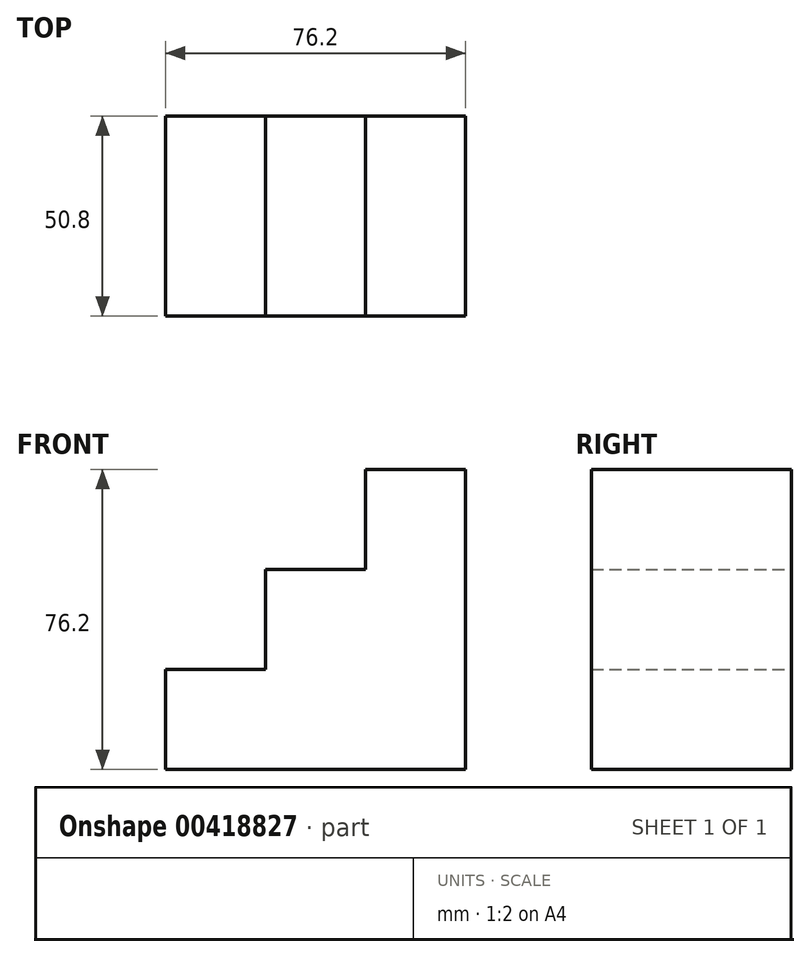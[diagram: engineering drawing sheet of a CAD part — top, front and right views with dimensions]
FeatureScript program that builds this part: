
annotation { "Feature Type Name" : "Feature", "Feature Type Description" : "" }
export const myFeature = defineFeature(function(context is Context, id is Id, definition is map)
    precondition{}
    {
        {
            var Q0;
            Q0=qCreatedBy(makeId("Front.planeOp"),FACE);
            var sketch = newSketch(context, id + "F0", { "sketchPlane" : qUnion([Q0])});
            skLineSegment(sketch, "E0", {"start": v(0, 0) * mm, "end": v(-76.2, 0) * mm});
            skLineSegment(sketch, "E1", {"start": v(0, 0) * mm, "end": v(0, 76.2) * mm});
            skLineSegment(sketch, "E2", {"start": v(-76.2, 0) * mm, "end": v(-76.2, 25.4) * mm});
            skLineSegment(sketch, "E3", {"start": v(-76.2, 25.4) * mm, "end": v(-50.8, 25.4) * mm});
            skLineSegment(sketch, "E4", {"start": v(-50.8, 25.4) * mm, "end": v(-50.8, 50.8) * mm});
            skLineSegment(sketch, "E5", {"start": v(-50.8, 50.8) * mm, "end": v(-25.4, 50.8) * mm});
            skLineSegment(sketch, "E6", {"start": v(-25.4, 50.8) * mm, "end": v(-25.4, 76.2) * mm});
            skLineSegment(sketch, "E7", {"start": v(-25.4, 76.2) * mm, "end": v(0, 76.2) * mm});
            skSolve(sketch);
        }
        {
            var Q0;
            Q0 = qSketchRegion(id + "F0", true);
            extrude(context, id + "F1", {"entities" : qUnion([Q0]), "depth" : 50.8 * mm});
        }
    });
